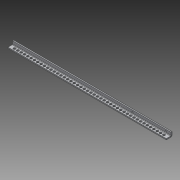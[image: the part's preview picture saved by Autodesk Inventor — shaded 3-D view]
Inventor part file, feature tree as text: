
AUTODESK INVENTOR PART (.ipt)
format: ipt  version: 2014 SP1 (Build 180222100, 222)  size: 262,656 bytes
history: native  units: in
note: dims shown in document units (in); Inventor stores cm internally (conversion verified against a paired STEP export)
features: other x4, sheet_metal_op x3, sketch x3, reference x1
ambient origin geometry x8: Origin, YZ Plane, XZ Plane, XY Plane, X Axis, Y Axis, Z Axis, Center Point
bodies: Solid1 (feature_tree)
feature tree (11):
  sheet_metal_op  "Face1"
  sheet_metal_op  "Flange1"
  sketch  "Sketch1"  dims[d0=0.125in]
  other  "Plate1"
  sketch  "Sketch2"  dims[d1=0.125in]
  other  "Plate2"
  sheet_metal_op  "Bend1"
  sketch  "Sketch3"  dims[d2=0.0625in d3=0.25in d4=0.125in d5=0.5in d6=90.0deg d7=0.05in d8=0.5in d9=0.125in d10=0.125in d11=0.125in d12=0.0in]
  reference  "Reference1"
  other  "Cut1"
  other  "Definition1"
